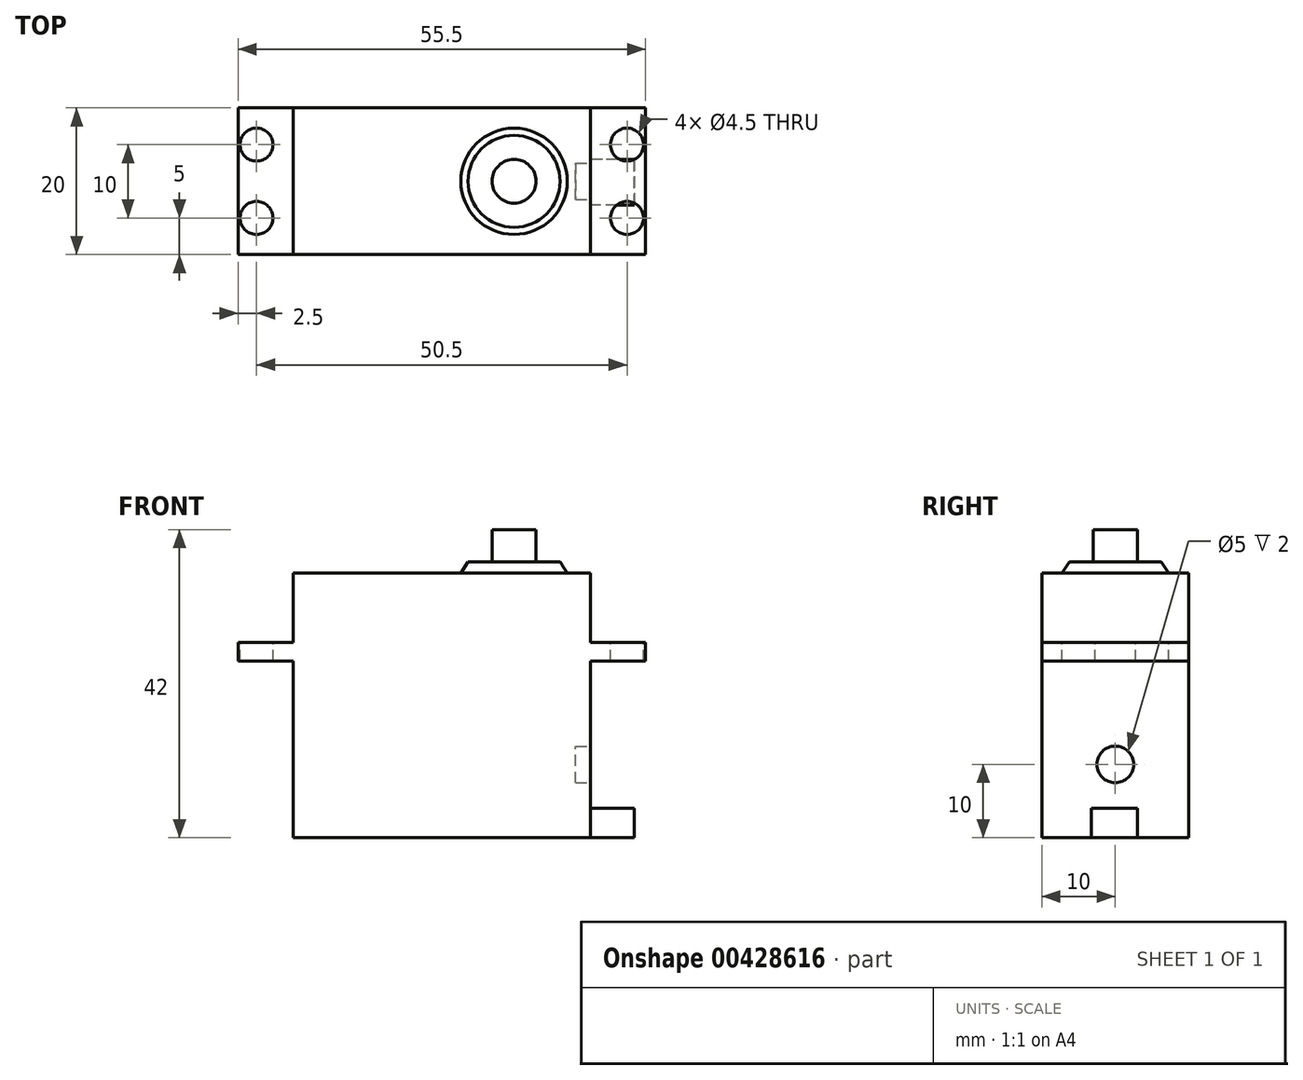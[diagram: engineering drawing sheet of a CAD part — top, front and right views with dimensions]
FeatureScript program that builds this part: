
annotation { "Feature Type Name" : "Feature", "Feature Type Description" : "" }
export const myFeature = defineFeature(function(context is Context, id is Id, definition is map)
    precondition{}
    {
        {
            var Q0;
            Q0=qCreatedBy(makeId("Front.planeOp"),FACE);
            var sketch = newSketch(context, id + "F0", { "sketchPlane" : qUnion([Q0])});
            skLineSegment(sketch, "E0.bottom", {"start": v(20.25, 18.05) * mm, "end": v(-20.25, 18.05) * mm});
            skLineSegment(sketch, "E0.top", {"start": v(20.25, -18.05) * mm, "end": v(-20.25, -18.05) * mm});
            skLineSegment(sketch, "E0.left", {"start": v(20.25, 18.05) * mm, "end": v(20.25, -18.05) * mm});
            skLineSegment(sketch, "E0.right", {"start": v(-20.25, 18.05) * mm, "end": v(-20.25, -18.05) * mm});
            skPoint(sketch, "E0.middle", {"position": v(0, 0) * mm});
            skSolve(sketch);
        }
        {
            var Q0;
            Q0 = qSketchRegion(id + "F0", true);
            var Q1;
            Q1 = qSketchRegion(id + "F5", true);
            extrude(context, id + "F1", {"entities" : qUnion([Q0, Q1]), "endBound" : BoundingType.SYMMETRIC, "depth" : 20 * mm});
        }
        {
            var Q0;
            Q0=makeQuery(id+"F1.opExtrude","SWEPT_FACE",FACE,{"disambiguationData":[OSD([sQuery(id+"F0.wireOp",EDGE,"E0.top")])]});
            cPlane(context, id + "F2", {"entities" : qUnion([Q0]), "cplaneType" : CPlaneType.OFFSET, "offset" : 26.6 * mm, "oppositeDirection" : true, "width" : 152.4 * mm, "height" : 152.4 * mm});
        }
        {
            var Q0;
            Q0=qCreatedBy(id+"F2.planeOp",FACE);
            var sketch = newSketch(context, id + "F3", { "sketchPlane" : qUnion([Q0])});
            skLineSegment(sketch, "E1.bottom", {"start": v(-20.25, 10) * mm, "end": v(-27.75, 10) * mm});
            skLineSegment(sketch, "E1.top", {"start": v(-20.25, -10) * mm, "end": v(-27.75, -10) * mm});
            skLineSegment(sketch, "E1.left", {"start": v(-20.25, 10) * mm, "end": v(-20.25, -10) * mm});
            skLineSegment(sketch, "E1.right", {"start": v(-27.75, 10) * mm, "end": v(-27.75, -10) * mm});
            skLineSegment(sketch, "E2", {"start": v(-27.75, 0) * mm, "end": v(-20.25, 0) * mm, "construction": true});
            skCircle(sketch, "E3", {"center": v(-25.25, 5) * mm, "radius": 2.25 * mm});
            skCircle(sketch, "E4.MirrorC", {"center": v(-25.25, -5) * mm, "radius": 2.25 * mm});
            skLineSegment(sketch, "E5.MirrorCS", {"start": v(20.25, 10) * mm, "end": v(27.75, 10) * mm});
            skLineSegment(sketch, "E6.MirrorCS", {"start": v(20.25, -10) * mm, "end": v(27.75, -10) * mm});
            skLineSegment(sketch, "E7.MirrorCS", {"start": v(20.25, 10) * mm, "end": v(20.25, -10) * mm});
            skLineSegment(sketch, "E8.MirrorCS", {"start": v(27.75, 10) * mm, "end": v(27.75, -10) * mm});
            skLineSegment(sketch, "E9.MirrorCS", {"start": v(27.75, 0) * mm, "end": v(20.25, 0) * mm, "construction": true});
            skCircle(sketch, "E10.MirrorC", {"center": v(25.25, 5) * mm, "radius": 2.25 * mm});
            skCircle(sketch, "E11.MirrorC", {"center": v(25.25, -5) * mm, "radius": 2.25 * mm});
            skSolve(sketch);
        }
        {
            var Q0;
            Q0 = qSketchRegion(id + "F3", true);
            extrude(context, id + "F4", {"entities" : qUnion([Q0]), "operationType" : NewBodyOperationType.ADD, "depth" : 2.5 * mm});
        }
        {
            var Q0;
            Q0=makeQuery(id+"F1.opExtrude","SWEPT_FACE",FACE,{"disambiguationData":[OSD([sQuery(id+"F0.wireOp",EDGE,"E0.bottom")])]});
            var sketch = newSketch(context, id + "F5", { "sketchPlane" : qUnion([Q0])});
            skLineSegment(sketch, "E12", {"start": v(-20.25, 0) * mm, "end": v(20.25, 0) * mm, "construction": true});
            skCircle(sketch, "E13", {"center": v(9.85, 0) * mm, "radius": 7.25 * mm});
            skSolve(sketch);
        }
        {
            var Q0;
            Q0 = qSketchRegion(id + "F5", true);
            extrude(context, id + "F6", {"entities" : qUnion([Q0]), "operationType" : NewBodyOperationType.ADD, "depth" : 1.5 * mm, "hasDraft" : true, "draftAngle" : 33 * degree, "draftPullDirection" : true});
        }
        {
            var Q0;
            Q0=makeQuery(id+"F1.opExtrude","SWEPT_FACE",FACE,{"disambiguationData":[OSD([sQuery(id+"F0.wireOp",EDGE,"E0.top")])]});
            cPlane(context, id + "F7", {"entities" : qUnion([Q0]), "cplaneType" : CPlaneType.OFFSET, "offset" : 42 * mm, "oppositeDirection" : true, "width" : 152.4 * mm, "height" : 152.4 * mm});
        }
        {
            var Q0;
            Q0=makeQuery(id+"F6.opExtrude","CAP_FACE",FACE,{"disambiguationData":[OSD([sQuery(id+"F5.wireOp",EDGE,"E13")])],"isStart":false});
            var sketch = newSketch(context, id + "F8", { "sketchPlane" : qUnion([Q0])});
            skCircle(sketch, "E14", {"center": v(9.85, 0) * mm, "radius": 3 * mm});
            skSolve(sketch);
        }
        {
            var Q0;
            Q0 = qSketchRegion(id + "F8", true);
            var Q1;
            Q1=qCreatedBy(id+"F7.planeOp",FACE);
            extrude(context, id + "F9", {"entities" : qUnion([Q0]), "operationType" : NewBodyOperationType.ADD, "endBound" : BoundingType.UP_TO_SURFACE, "endBoundEntityFace" : qUnion([Q1]), "depth" : 25.4 * mm});
        }
        {
            var Q0;
            {var subQ1=sQuery(id+"F0.wireOp",EDGE,"E0.top");var subQ3=sQuery(id+"F0.wireOp",EDGE,"E0.left");Q0=makeQuery(id+"F4.boolean.opBoolean","SPLIT",FACE,{"disambiguationData":[TD([makeQuery(id+"F1.opExtrude","SWEPT_FACE",FACE,{"disambiguationData":[OSD([subQ1])]})])],"derivedFrom":makeQuery(id+"F1.opExtrude","SWEPT_FACE",FACE,{"disambiguationData":[OSD([subQ3])]})});}
            var sketch = newSketch(context, id + "F10", { "sketchPlane" : qUnion([Q0])});
            skLineSegment(sketch, "E15", {"start": v(0, 0) * mm, "end": v(0, -18.05) * mm, "construction": true});
            skCircle(sketch, "E16", {"center": v(0, -8.05) * mm, "radius": 2.5 * mm});
            skSolve(sketch);
        }
        {
            var Q0;
            Q0 = qSketchRegion(id + "F10", true);
            extrude(context, id + "F11", {"entities" : qUnion([Q0]), "operationType" : NewBodyOperationType.REMOVE, "oppositeDirection" : true, "depth" : 2 * mm});
        }
        {
            var Q0;
            {var subQ1=sQuery(id+"F0.wireOp",EDGE,"E0.top");var subQ3=sQuery(id+"F0.wireOp",EDGE,"E0.left");Q0=makeQuery(id+"F4.boolean.opBoolean","SPLIT",FACE,{"disambiguationData":[TD([makeQuery(id+"F1.opExtrude","SWEPT_FACE",FACE,{"disambiguationData":[OSD([subQ1])]})])],"derivedFrom":makeQuery(id+"F1.opExtrude","SWEPT_FACE",FACE,{"disambiguationData":[OSD([subQ3])]})});}
            var sketch = newSketch(context, id + "F12", { "sketchPlane" : qUnion([Q0])});
            skLineSegment(sketch, "E17", {"start": v(0, 0) * mm, "end": v(0, -18.05) * mm, "construction": true});
            skLineSegment(sketch, "E18.bottom", {"start": v(3, -18.05) * mm, "end": v(-3.25, -18.05) * mm});
            skLineSegment(sketch, "E18.top", {"start": v(3, -14.05) * mm, "end": v(-3.25, -14.05) * mm});
            skLineSegment(sketch, "E18.left", {"start": v(3, -18.05) * mm, "end": v(3, -14.05) * mm});
            skLineSegment(sketch, "E18.right", {"start": v(-3.25, -18.05) * mm, "end": v(-3.25, -14.05) * mm});
            skSolve(sketch);
        }
        {
            var Q0;
            Q0 = qSketchRegion(id + "F12", true);
            extrude(context, id + "F13", {"entities" : qUnion([Q0]), "operationType" : NewBodyOperationType.ADD, "depth" : 6 * mm});
        }
    });
